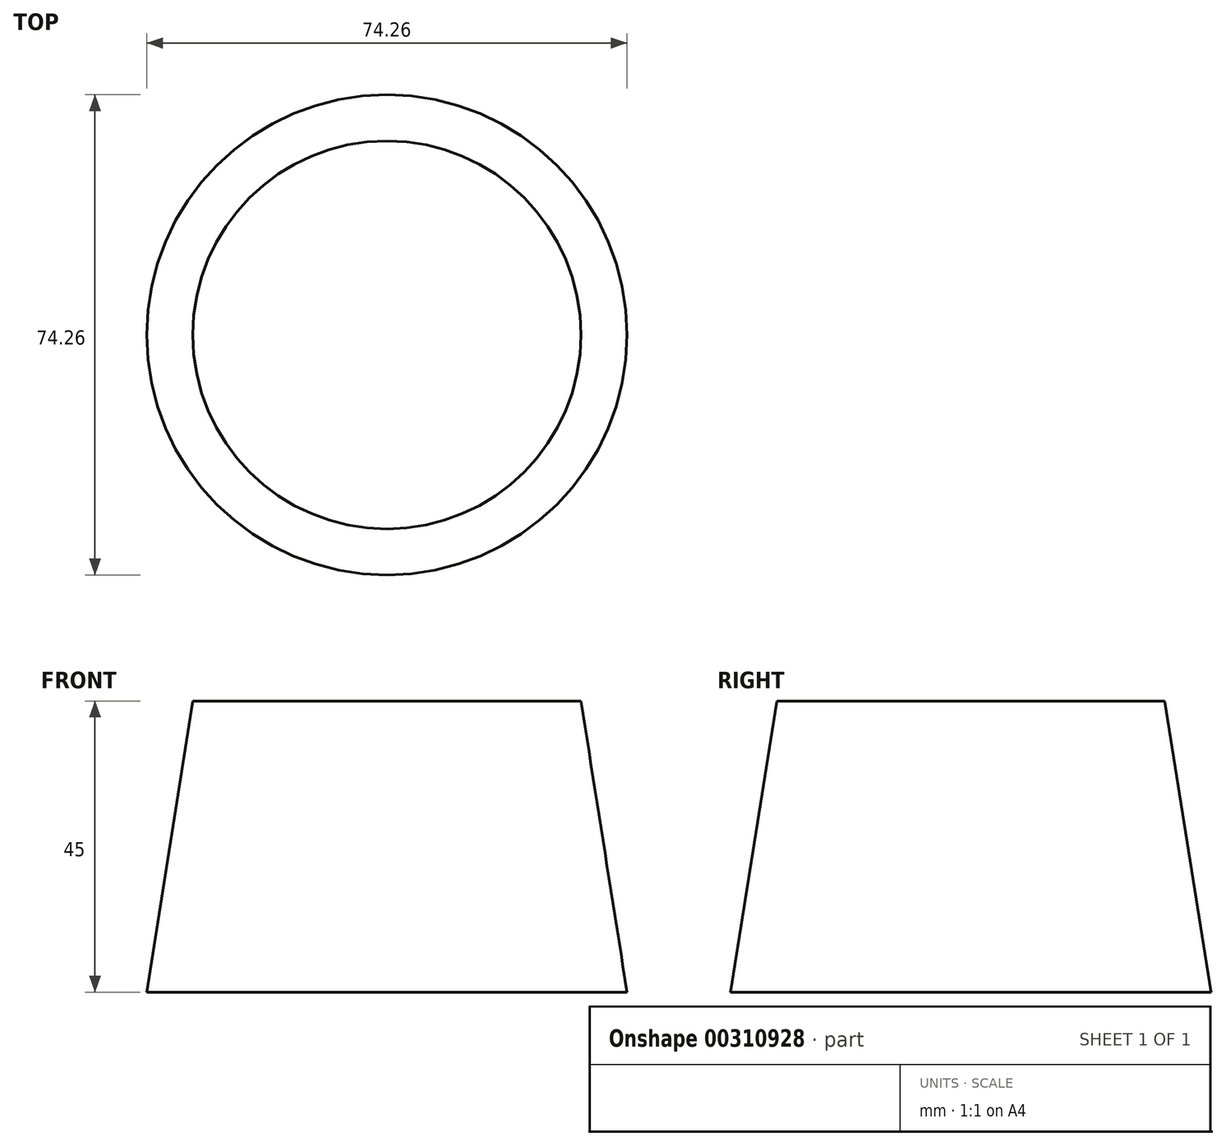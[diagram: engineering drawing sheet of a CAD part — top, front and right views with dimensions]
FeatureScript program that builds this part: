
annotation { "Feature Type Name" : "Feature", "Feature Type Description" : "" }
export const myFeature = defineFeature(function(context is Context, id is Id, definition is map)
    precondition{}
    {
        {
            var Q0;
            Q0=qCreatedBy(makeId("Top.planeOp"),FACE);
            var sketch = newSketch(context, id + "F0", { "sketchPlane" : qUnion([Q0])});
            skCircle(sketch, "E0", {"center": v(0, 0) * mm, "radius": 30 * mm});
            skSolve(sketch);
        }
        {
            var Q0;
            Q0=makeQuery(id+"F0.imprint","IMPRINT",FACE,{"disambiguationData":[TD([[makeQuery(id+"F0.imprint","IMPRINT",EDGE,{"derivedFrom":sQuery(id+"F0.wireOp",EDGE,"E0")}),1.0]])]});
            extrude(context, id + "F1", {"entities" : qUnion([Q0]), "oppositeDirection" : true, "depth" : 45 * mm, "hasDraft" : true, "draftAngle" : 9 * degree});
        }
    });
